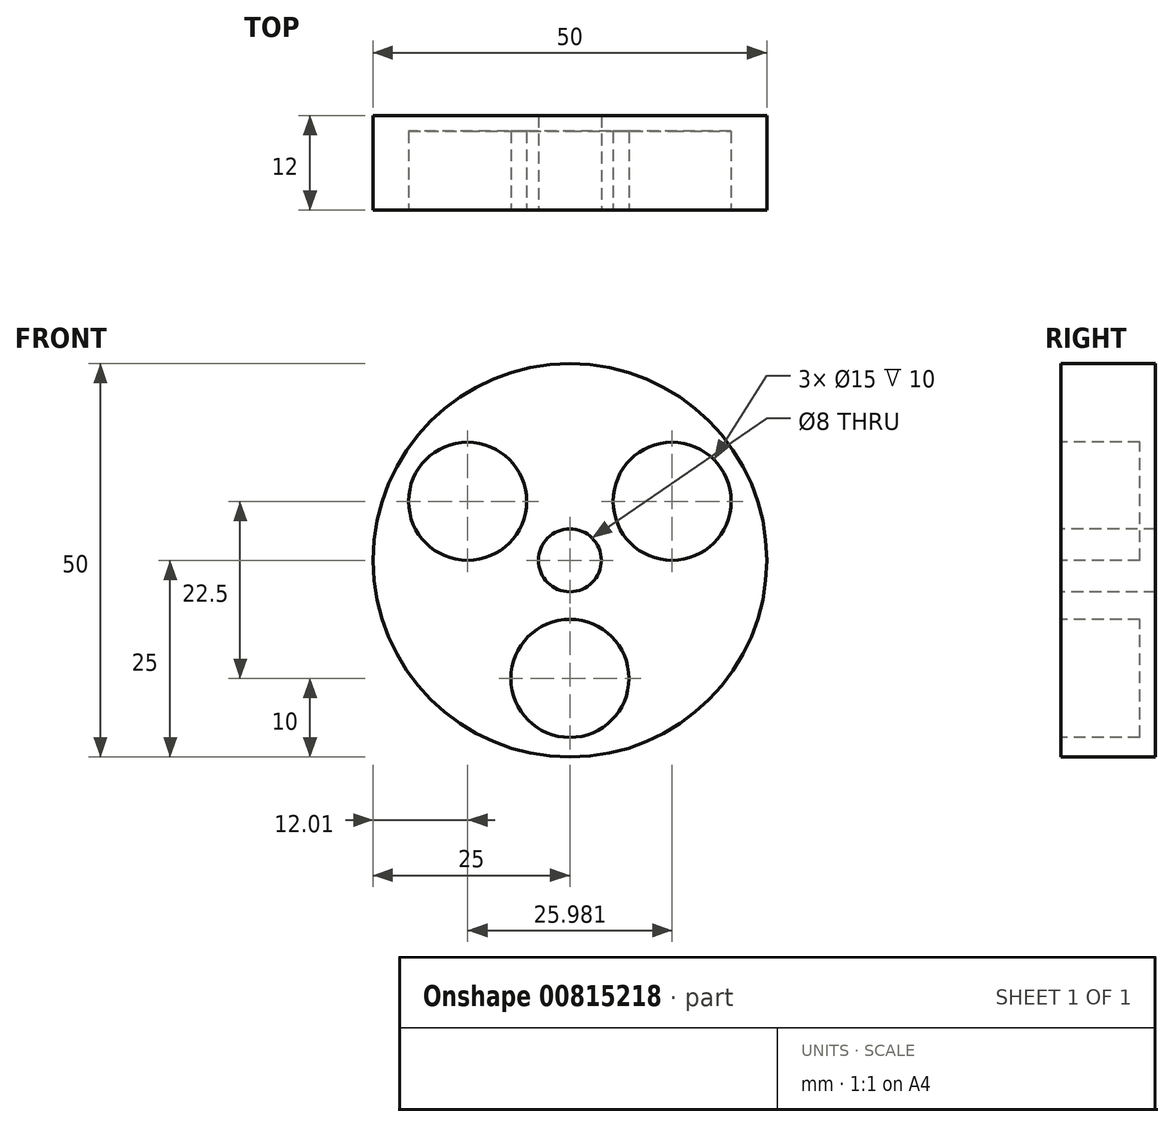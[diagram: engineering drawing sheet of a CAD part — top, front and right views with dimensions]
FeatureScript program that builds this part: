
annotation { "Feature Type Name" : "Feature", "Feature Type Description" : "" }
export const myFeature = defineFeature(function(context is Context, id is Id, definition is map)
    precondition{}
    {
        {
            var Q0;
            Q0=qCreatedBy(makeId("Front.planeOp"),FACE);
            var sketch = newSketch(context, id + "F0", { "sketchPlane" : qUnion([Q0])});
            skCircle(sketch, "E0", {"center": v(0, 0) * mm, "radius": 25 * mm});
            skCircle(sketch, "E1", {"center": v(0, 0) * mm, "radius": 15 * mm, "construction": true});
            skCircle(sketch, "E2", {"center": v(0, 0) * mm, "radius": 20 * mm, "construction": true});
            skCircle(sketch, "E3", {"center": v(0, -15) * mm, "radius": 7.5 * mm});
            skCircle(sketch, "E4", {"center": v(0, -15) * mm, "radius": 5 * mm, "construction": true});
            skCircle(sketch, "E5.1.0", {"center": v(13, 7.5) * mm, "radius": 5 * mm, "construction": true});
            skCircle(sketch, "E5.1.1", {"center": v(13, 7.5) * mm, "radius": 7.5 * mm});
            skCircle(sketch, "E5.2.0", {"center": v(-13, 7.5) * mm, "radius": 5 * mm, "construction": true});
            skCircle(sketch, "E5.2.1", {"center": v(-13, 7.5) * mm, "radius": 7.5 * mm});
            skCircle(sketch, "E6", {"center": v(0, 0) * mm, "radius": 4 * mm});
            skSolve(sketch);
        }
        {
            var Q0;
            Q0=makeQuery(id+"F0.imprint","IMPRINT",FACE,{"disambiguationData":[TD([[makeQuery(id+"F0.imprint","IMPRINT",EDGE,{"derivedFrom":sQuery(id+"F0.wireOp",EDGE,"E0")}),1.0]])]});
            extrude(context, id + "F1", {"entities" : qUnion([Q0]), "oppositeDirection" : true, "depth" : 10 * mm, "offsetDistance" : 25 * mm});
        }
        {
            var Q0;
            Q0=makeQuery(id+"F1.opExtrude","CAP_FACE",FACE,{"disambiguationData":[OSD([sQuery(id+"F0.wireOp",EDGE,"E0"),sQuery(id+"F0.wireOp",EDGE,"E3"),sQuery(id+"F0.wireOp",EDGE,"E5.1.1"),sQuery(id+"F0.wireOp",EDGE,"E5.2.1"),sQuery(id+"F0.wireOp",EDGE,"E6")])],"isStart":false});
            var sketch = newSketch(context, id + "F2", { "sketchPlane" : qUnion([Q0])});
            skCircle(sketch, "E7.0", {"center": v(0, 0) * mm, "radius": 25 * mm});
            skSolve(sketch);
        }
        {
            var Q0;
            Q0 = qSketchRegion(id + "F2", true);
            extrude(context, id + "F3", {"entities" : qUnion([Q0]), "operationType" : NewBodyOperationType.ADD, "depth" : 2 * mm, "offsetDistance" : 25 * mm});
        }
        {
            var Q0;
            Q0=makeQuery(id+"F0.imprint","IMPRINT",FACE,{"disambiguationData":[TD([[makeQuery(id+"F0.imprint","IMPRINT",EDGE,{"derivedFrom":sQuery(id+"F0.wireOp",EDGE,"E6")}),1.0]])]});
            extrude(context, id + "F4", {"entities" : qUnion([Q0]), "operationType" : NewBodyOperationType.REMOVE, "oppositeDirection" : true, "depth" : 25 * mm, "offsetDistance" : 25 * mm});
        }
    });
